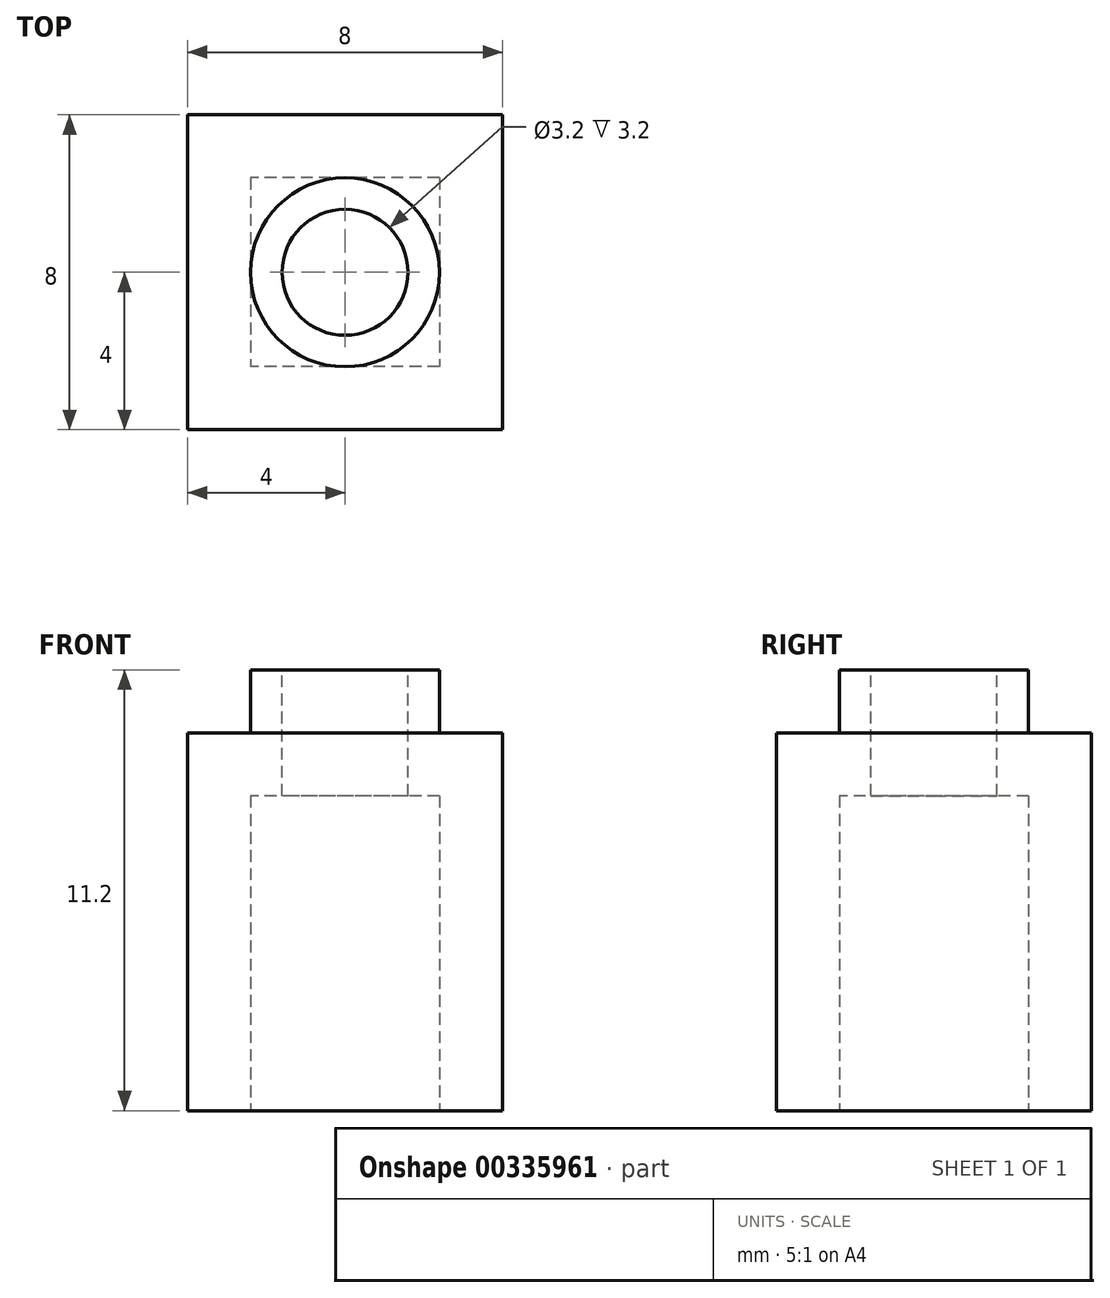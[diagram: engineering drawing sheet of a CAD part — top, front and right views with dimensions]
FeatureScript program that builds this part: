
annotation { "Feature Type Name" : "Feature", "Feature Type Description" : "" }
export const myFeature = defineFeature(function(context is Context, id is Id, definition is map)
    precondition{}
    {
        {
            var Q0;
            Q0=qCreatedBy(makeId("Front.planeOp"),FACE);
            var sketch = newSketch(context, id + "F0", { "sketchPlane" : qUnion([Q0])});
            skLineSegment(sketch, "E0.bottom", {"start": v(-4, 0) * mm, "end": v(4, 0) * mm});
            skLineSegment(sketch, "E0.top", {"start": v(-4, 9.6) * mm, "end": v(4, 9.6) * mm});
            skLineSegment(sketch, "E0.left", {"start": v(-4, 0) * mm, "end": v(-4, 9.6) * mm});
            skLineSegment(sketch, "E0.right", {"start": v(4, 0) * mm, "end": v(4, 9.6) * mm});
            skSolve(sketch);
        }
        {
            var Q0;
            Q0 = qSketchRegion(id + "F0", true);
            extrude(context, id + "F1", {"entities" : qUnion([Q0]), "endBound" : BoundingType.SYMMETRIC, "depth" : 8 * mm});
        }
        {
            var Q0;
            Q0=makeQuery(id+"F1.opExtrude","SWEPT_FACE",FACE,{"disambiguationData":[OSD([sQuery(id+"F0.wireOp",EDGE,"E0.bottom")])]});
            var sketch = newSketch(context, id + "F2", { "sketchPlane" : qUnion([Q0])});
            skLineSegment(sketch, "E1.bottom", {"start": v(2.4, -2.4) * mm, "end": v(-2.4, -2.4) * mm});
            skLineSegment(sketch, "E1.top", {"start": v(2.4, 2.4) * mm, "end": v(-2.4, 2.4) * mm});
            skLineSegment(sketch, "E1.left", {"start": v(2.4, -2.4) * mm, "end": v(2.4, 2.4) * mm});
            skLineSegment(sketch, "E1.right", {"start": v(-2.4, -2.4) * mm, "end": v(-2.4, 2.4) * mm});
            skPoint(sketch, "E1.middle", {"position": v(0, 0) * mm});
            skSolve(sketch);
        }
        {
            var Q0;
            Q0=makeQuery(id+"F2.imprint","IMPRINT",FACE,{"disambiguationData":[TD([[makeQuery(id+"F2.imprint","IMPRINT",EDGE,{"derivedFrom":sQuery(id+"F2.wireOp",EDGE,"E1.bottom")}),-1.0]])]});
            extrude(context, id + "F3", {"entities" : qUnion([Q0]), "operationType" : NewBodyOperationType.REMOVE, "oppositeDirection" : true, "depth" : 8 * mm});
        }
        {
            var Q0;
            Q0=makeQuery(id+"F1.opExtrude","SWEPT_FACE",FACE,{"disambiguationData":[OSD([sQuery(id+"F0.wireOp",EDGE,"E0.top")])]});
            var sketch = newSketch(context, id + "F4", { "sketchPlane" : qUnion([Q0])});
            skCircle(sketch, "E2", {"center": v(0, 0) * mm, "radius": 2.4 * mm});
            skCircle(sketch, "E3", {"center": v(0, 0) * mm, "radius": 1.6 * mm});
            skSolve(sketch);
        }
        {
            var Q0;
            Q0=makeQuery(id+"F4.imprint","IMPRINT",FACE,{"disambiguationData":[TD([[makeQuery(id+"F4.imprint","IMPRINT",EDGE,{"derivedFrom":sQuery(id+"F4.wireOp",EDGE,"E3")}),1.0]])]});
            extrude(context, id + "F5", {"entities" : qUnion([Q0]), "operationType" : NewBodyOperationType.REMOVE, "oppositeDirection" : true, "depth" : 1.6 * mm});
        }
        {
            var Q0;
            Q0=makeQuery(id+"F1.opExtrude","SWEPT_FACE",FACE,{"disambiguationData":[OSD([sQuery(id+"F0.wireOp",EDGE,"E0.top")])]});
            var sketch = newSketch(context, id + "F6", { "sketchPlane" : qUnion([Q0])});
            skCircle(sketch, "E4", {"center": v(0, 0) * mm, "radius": 2.4 * mm});
            skSolve(sketch);
        }
        {
            var Q0;
            Q0=makeQuery(id+"F6.imprint","IMPRINT",FACE,{"disambiguationData":[TD([[makeQuery(id+"F6.imprint","IMPRINT",EDGE,{"derivedFrom":sQuery(id+"F6.wireOp",EDGE,"E4")}),1.0]])]});
            var Q1;
            Q1=makeQuery(id+"F6.imprint","IMPRINT",FACE,{"disambiguationData":[TD([[makeQuery(id+"F6.imprint","IMPRINT",EDGE,{"derivedFrom":makeQuery(id+"F5.boolean.opBoolean","COPY",EDGE,{"derivedFrom":makeQuery(id+"F5.opExtrude","CAP_EDGE",EDGE,{"disambiguationData":[OSD([sQuery(id+"F4.wireOp",EDGE,"E3")])],"isStart":true})})}),1.0]])]});
            extrude(context, id + "F7", {"entities" : qUnion([Q0, Q1]), "operationType" : NewBodyOperationType.ADD, "depth" : 1.6 * mm});
        }
    });
